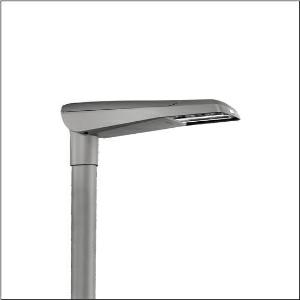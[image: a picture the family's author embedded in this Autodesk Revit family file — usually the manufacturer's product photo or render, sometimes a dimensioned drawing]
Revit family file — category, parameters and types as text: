
# Revit family: streetlight_sl_11_iq_micro___st1_2a_5xc1a41f08ce_4ecf
name_source: partatom
category: Lighting Fixtures
units: mm (PartAtom-declared; Revit-internal decimal feet)

## family parameters
Cut with Voids When Loaded = No
Host = Face
Light Source = No
Part Type = Normal
Room Calculation Point = No
Round Connector Dimension = Use Diameter
Shared = No

## types (1)
- --- (1 x LED, 1960 lm, 12.6 W, 4000K)
    Apparent Load = 13 VA
    CIE Flux Codes = 33 71 96 100 100
    Color Rendering = 70
    Color Temperature = 4000K
    Default Elevation = 1800 mm
    Description = Streetlight SL 11 iQ micro, mast luminaire, primary light control with 3 zone facetted reflector, of plastic, silver coated, highly specular, primary optical cover: cover, of PMMA, transparent, light distribution: ST1.2a, light emission: direct distribution, primary light characteristic: asymmetric, installation type: post-top, side-entry, lamps: LED, High Power LED, rated values: 1.960lm | 12,6W | 155,6lm/W (begin service life); end service life: 1.960lm | 12,9W; at 50% lumin. flux: 980lm | 6,8W | 144,1lm/W, colour temperature: 4000K, colour rendering: CRI > 70, light colour: 740, light setting 1 begin service life: 100% | 1.960lm | 12,6W | 155,6lm/W | 4.000K, light setting 1 end service life: 12,9W, further light settings possible, control: Street-Remote, optimised constant luminous flux control (CLO 2.0), Desk-Remote (wireless, voltage-free reading and setting of iQ features in the workshop via application-optimized NFC function/RFID function), Light-Fading, Smart-Wire, Night-Set, Lumen-Switch, Temp-Guard, Auto-Match, with cable H07RN-F 3x 1.5mm², mains connection: 230..240V, AC, 50/60Hz, connection cable pre-assembled, cable length: 5,5m, luminaire housing, of diecast aluminium, powder-coated, SITECO metallic grey (DB 702S), please order mast flange separately, inclination adjustable without tools: 0°, 5°, 10°, 15° (post-top) | 0°, -5°, -10°, -15° (side-entry), sealing non-destructively replaceable, multi-level sealing system, length: 600mm, width: 174mm, height: 116mm, mast flange for spigot size: 42mm (side-entry): 5XC10008XM4, 60/48mm (side-entry/post-top): 5XC10108XM2, 76/60mm (side-entry/post-top): 5XC10108XM1, equipment: standard, protection rating (complete): IP66, insulation class (complete): insulation class II (safety insulation), certification: CE, ENEC, ENEC+, VDE, impact resistance: IK10, permissible operating ambient temperature for outdoor applications: -25..+50°C, standard-compliant lighting for roads and squares, Environmental Product Declaration (EPD) tested and certified by an independent institute, packaging unit: 1 piece

Light Distribution: ST1.2a
    Height = 116 mm
    Lamp = 1 x LED
    Lamp Light Flux = 1960 lm
    Lamp Power = 12.6 W
    Lamp count = 1
    Length = 600 mm
    Luminous efficacy = 156 lm/W
    Manufacturer = Siteco
    ModVariant = No
    Model = 5XC1A41F08CE
    Mounting Place = Pole
    Mounting Type = Pole top
    Number of Poles = 1
    OnlyDefault = Yes
    Power Factor = 1
    Product Name = Streetlight SL 11 iQ micro | ST1.2a
    Product group = mast luminaire | pylon top
    ProductGroupID = 6100
    Protection Class = Protection class II
    Protection Degree = IP 66
    RLX_Detail_Level = 1
    RLX_Emergency_Light_Flux = 0 lm
    RLX_Emergency_Type = 0
    RLX_Emergency_Type_DB = No
    RlxData = <blob elided: 26477 chars, md5=d13f8241>
    Socket = socket
    Standby Power = 0 W
    System Light Flux = 1960 lm
    System Power = 13 W
    Type Comments = factory setting: luminous flux: 100 % | dim-lin: 254 | 229 mA
    Type Image = l_1006566.jpg
    URL = http://relux.com
    VarID = @adj_020737
    Voltage = 0 V
    Weight = 0.00 kg
    Width = 174 mm

## geometry (parser evidence)
native form markers: Blend x4, Sweep x10
no freeform markers — native parametric forms only
